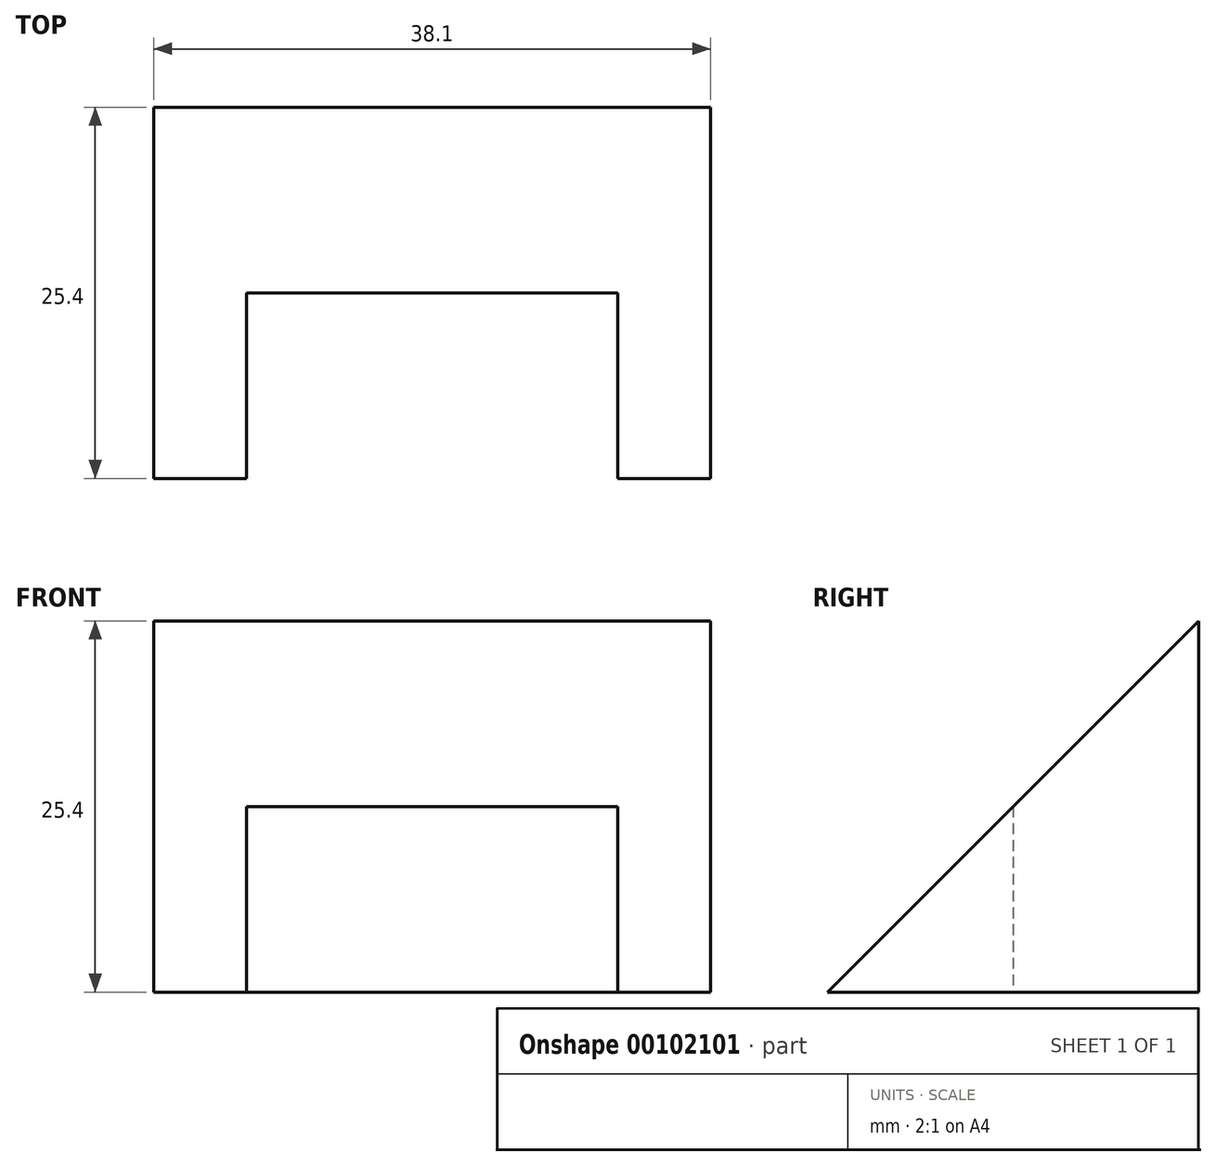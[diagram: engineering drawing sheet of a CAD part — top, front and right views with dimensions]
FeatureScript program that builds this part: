
annotation { "Feature Type Name" : "Feature", "Feature Type Description" : "" }
export const myFeature = defineFeature(function(context is Context, id is Id, definition is map)
    precondition{}
    {
        {
            var Q0;
            Q0=qCreatedBy(makeId("Right.planeOp"),FACE);
            var sketch = newSketch(context, id + "F0", { "sketchPlane" : qUnion([Q0])});
            skLineSegment(sketch, "E0", {"start": v(0, 0) * mm, "end": v(25.4, 0) * mm});
            skLineSegment(sketch, "E1", {"start": v(25.4, 0) * mm, "end": v(25.4, 25.4) * mm});
            skLineSegment(sketch, "E2", {"start": v(25.4, 25.4) * mm, "end": v(0, 0) * mm});
            skSolve(sketch);
        }
        {
            var Q0;
            Q0 = qSketchRegion(id + "F0", true);
            extrude(context, id + "F1", {"entities" : qUnion([Q0]), "endBound" : BoundingType.SYMMETRIC, "depth" : 38.1 * mm});
        }
        {
            var Q0;
            Q0=qCreatedBy(makeId("Top.planeOp"),FACE);
            var sketch = newSketch(context, id + "F2", { "sketchPlane" : qUnion([Q0])});
            skLineSegment(sketch, "E3.bottom", {"start": v(-12.7, 0) * mm, "end": v(12.7, 0) * mm});
            skLineSegment(sketch, "E3.top", {"start": v(-12.7, 12.7) * mm, "end": v(12.7, 12.7) * mm});
            skLineSegment(sketch, "E3.left", {"start": v(-12.7, 0) * mm, "end": v(-12.7, 12.7) * mm});
            skLineSegment(sketch, "E3.right", {"start": v(12.7, 0) * mm, "end": v(12.7, 12.7) * mm});
            skSolve(sketch);
        }
        {
            var Q0;
            Q0 = qSketchRegion(id + "F2", true);
            extrude(context, id + "F3", {"entities" : qUnion([Q0]), "operationType" : NewBodyOperationType.REMOVE, "endBound" : BoundingType.THROUGH_ALL, "depth" : 25.4 * mm});
        }
    });
